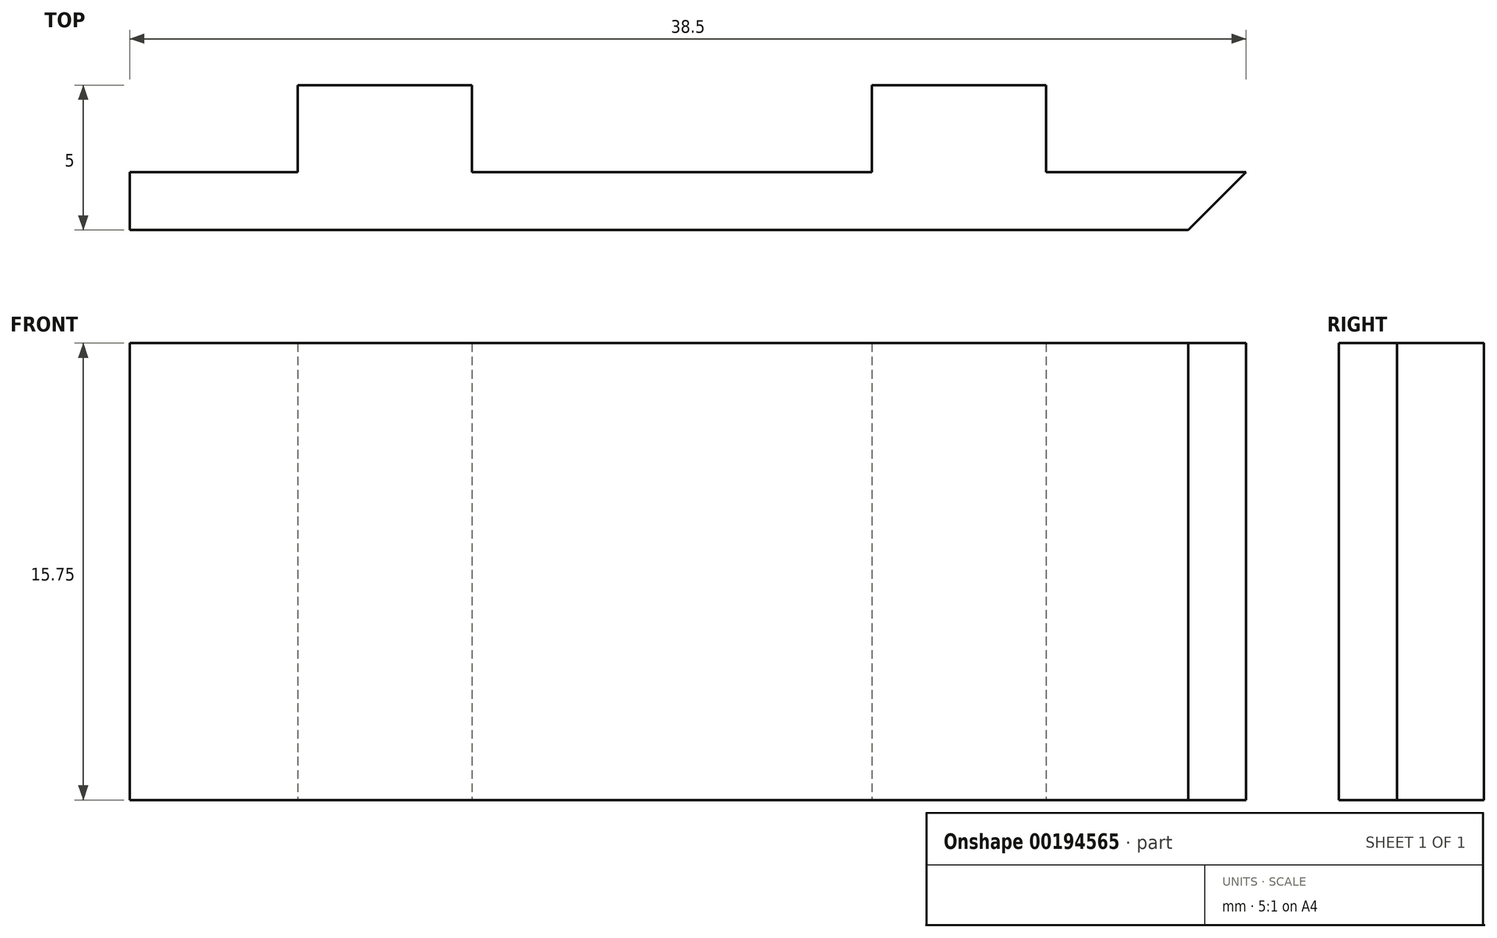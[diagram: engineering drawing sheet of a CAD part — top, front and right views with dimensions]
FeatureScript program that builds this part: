
annotation { "Feature Type Name" : "Feature", "Feature Type Description" : "" }
export const myFeature = defineFeature(function(context is Context, id is Id, definition is map)
    precondition{}
    {
        {
            var Q0;
            Q0=qCreatedBy(makeId("Top.planeOp"),FACE);
            var sketch = newSketch(context, id + "F0", { "sketchPlane" : qUnion([Q0])});
            skLineSegment(sketch, "E0", {"start": v(44.5, 0) * mm, "end": v(44.5, 10) * mm});
            skLineSegment(sketch, "E1", {"start": v(44.5, 10) * mm, "end": v(37.6, 10) * mm});
            skLineSegment(sketch, "E2", {"start": v(37.6, 10) * mm, "end": v(37.6, 16) * mm});
            skLineSegment(sketch, "E3", {"start": v(37.6, 16) * mm, "end": v(31.6, 16) * mm});
            skLineSegment(sketch, "E4", {"start": v(31.6, 16) * mm, "end": v(31.6, 10) * mm});
            skLineSegment(sketch, "E5", {"start": v(31.6, 10) * mm, "end": v(17.8, 10) * mm});
            skLineSegment(sketch, "E6", {"start": v(17.8, 10) * mm, "end": v(17.8, 16) * mm});
            skLineSegment(sketch, "E7", {"start": v(17.8, 16) * mm, "end": v(11.8, 16) * mm});
            skLineSegment(sketch, "E8", {"start": v(11.8, 16) * mm, "end": v(11.8, 10) * mm});
            skLineSegment(sketch, "E9", {"start": v(11.8, 10) * mm, "end": v(0, 10) * mm});
            skLineSegment(sketch, "E10", {"start": v(0, 0) * mm, "end": v(44.5, 0) * mm});
            skLineSegment(sketch, "E11", {"start": v(0, 10) * mm, "end": v(0, 0) * mm});
            skSolve(sketch);
        }
        {
            var Q0;
            Q0 = qSketchRegion(id + "F0", true);
            extrude(context, id + "F1", {"entities" : qUnion([Q0]), "depth" : 15.75 * mm});
        }
        {
            var Q0;
            Q0=makeQuery(id+"F1.opExtrude","CAP_FACE",FACE,{"disambiguationData":[OSD([sQuery(id+"F0.wireOp",EDGE,"E0"),sQuery(id+"F0.wireOp",EDGE,"E1"),sQuery(id+"F0.wireOp",EDGE,"E2"),sQuery(id+"F0.wireOp",EDGE,"E3"),sQuery(id+"F0.wireOp",EDGE,"E4"),sQuery(id+"F0.wireOp",EDGE,"E5"),sQuery(id+"F0.wireOp",EDGE,"E6"),sQuery(id+"F0.wireOp",EDGE,"E7"),sQuery(id+"F0.wireOp",EDGE,"E8"),sQuery(id+"F0.wireOp",EDGE,"E9"),sQuery(id+"F0.wireOp",EDGE,"E10"),sQuery(id+"F0.wireOp",EDGE,"E11")])],"isStart":false});
            var sketch = newSketch(context, id + "F2", { "sketchPlane" : qUnion([Q0])});
            skPoint(sketch, "E12", {"position": v(24.7, 5) * mm});
            skPoint(sketch, "E12.positionSnap0", {"position": v(44.5, 5) * mm});
            skPoint(sketch, "E12.positionSnap1", {"position": v(24.7, 10) * mm});
            skSolve(sketch);
        }
        {
            var Q0;
            Q0=sQuery(id+"F2.wireOp",VERTEX,"E12");
            var Q1;
            Q1=makeQuery(id+"F1.opExtrude","SWEPT_BODY",BODY,{"disambiguationData":[OSD([sQuery(id+"F0.wireOp",EDGE,"E0"),sQuery(id+"F0.wireOp",EDGE,"E1"),sQuery(id+"F0.wireOp",EDGE,"E2"),sQuery(id+"F0.wireOp",EDGE,"E3"),sQuery(id+"F0.wireOp",EDGE,"E4"),sQuery(id+"F0.wireOp",EDGE,"E5"),sQuery(id+"F0.wireOp",EDGE,"E6"),sQuery(id+"F0.wireOp",EDGE,"E7"),sQuery(id+"F0.wireOp",EDGE,"E8"),sQuery(id+"F0.wireOp",EDGE,"E9"),sQuery(id+"F0.wireOp",EDGE,"E10"),sQuery(id+"F0.wireOp",EDGE,"E11")])]});
            hole(context, id + "F3", {"style" : HoleStyle.SIMPLE, "endStyle" : HoleEndStyle.THROUGH, "holeDiameter" : 4 * mm, "locations" : qUnion([Q0]), "scope" : qUnion([Q1]), "isTappedThrough" : true, "startStyle" : HoleStartStyle.PART});
        }
        {
            var Q0;
            Q0=makeQuery(id+"F1.opExtrude","SWEPT_FACE",FACE,{"disambiguationData":[OSD([sQuery(id+"F0.wireOp",EDGE,"E11")])]});
            extrude(context, id + "F4", {"entities" : qUnion([Q0]), "operationType" : NewBodyOperationType.ADD, "depth" : 3 * mm});
        }
        {
            var Q0;
            {var subQ0=sQuery(id+"F0.wireOp",EDGE,"E9");Q0=makeQuery(id+"F4.boolean.opBoolean","MERGE",FACE,{"derivedFrom":[makeQuery(id+"F1.opExtrude","SWEPT_FACE",FACE,{"disambiguationData":[OSD([subQ0])]}),makeQuery(id+"F4.opExtrude","SWEPT_FACE",FACE,{"disambiguationData":[OSD([subQ0,sQuery(id+"F0.wireOp",EDGE,"E11")])]})]});}
            var sketch = newSketch(context, id + "F5", { "sketchPlane" : qUnion([Q0])});
            skLineSegment(sketch, "E13", {"start": v(0, 0) * mm, "end": v(0, 15.75) * mm});
            skSolve(sketch);
        }
        {
            var Q0;
            {var subQ0=sQuery(id+"F5.wireOp",EDGE,"E13");Q0=makeQuery(id+"F5.imprint","IMPRINT",FACE,{"disambiguationData":[TD([[makeQuery(id+"F5.imprint","IMPRINT",EDGE,{"derivedFrom":subQ0}),-1.0]])]});}
            extrude(context, id + "F6", {"entities" : qUnion([Q0]), "operationType" : NewBodyOperationType.ADD, "depth" : 25 * mm});
        }
        {
            var Q0;
            Q0=makeQuery(id+"F6.opExtrude","SWEPT_FACE",FACE,{"disambiguationData":[OSD([sQuery(id+"F5.wireOp",EDGE,"E13")])]});
            var sketch = newSketch(context, id + "F7", { "sketchPlane" : qUnion([Q0])});
            skPoint(sketch, "E14", {"position": v(27.25, 7.88) * mm});
            skPoint(sketch, "E14.positionSnap0", {"position": v(35, 7.88) * mm});
            skPoint(sketch, "E15", {"position": v(17.75, 7.88) * mm});
            skLineSegment(sketch, "E16", {"start": v(27.25, 7.88) * mm, "end": v(35, 7.88) * mm, "construction": true});
            skLineSegment(sketch, "E17", {"start": v(17.75, 7.88) * mm, "end": v(10, 7.88) * mm, "construction": true});
            skSolve(sketch);
        }
        {
            var Q0;
            Q0=sQuery(id+"F7.wireOp",VERTEX,"E14");
            var Q1;
            Q1=sQuery(id+"F7.wireOp",VERTEX,"E15");
            var Q2;
            Q2=makeQuery(id+"F1.opExtrude","SWEPT_BODY",BODY,{"disambiguationData":[OSD([sQuery(id+"F0.wireOp",EDGE,"E0"),sQuery(id+"F0.wireOp",EDGE,"E1"),sQuery(id+"F0.wireOp",EDGE,"E2"),sQuery(id+"F0.wireOp",EDGE,"E3"),sQuery(id+"F0.wireOp",EDGE,"E4"),sQuery(id+"F0.wireOp",EDGE,"E5"),sQuery(id+"F0.wireOp",EDGE,"E6"),sQuery(id+"F0.wireOp",EDGE,"E7"),sQuery(id+"F0.wireOp",EDGE,"E8"),sQuery(id+"F0.wireOp",EDGE,"E9"),sQuery(id+"F0.wireOp",EDGE,"E10"),sQuery(id+"F0.wireOp",EDGE,"E11")])]});
            hole(context, id + "F8", {"style" : HoleStyle.SIMPLE, "endStyle" : HoleEndStyle.THROUGH, "holeDiameter" : 2 * mm, "locations" : qUnion([Q0, Q1]), "scope" : qUnion([Q2]), "isTappedThrough" : true, "startStyle" : HoleStartStyle.SKETCH});
        }
        {
            var Q0;
            {var subQ0=sQuery(id+"F0.wireOp",EDGE,"E11");var subQ1=sQuery(id+"F0.wireOp",EDGE,"E9");var subQ2=makeQuery(id+"F4.boolean.opBoolean","MERGE",EDGE,{"derivedFrom":[makeQuery(id+"F1.opExtrude","CAP_EDGE",EDGE,{"disambiguationData":[OSD([subQ1])],"isStart":false}),makeQuery(id+"F4.opExtrude","SWEPT_EDGE",EDGE,{"disambiguationData":[OSD([subQ1,subQ0]),TDD([makeQuery(id+"F1.opExtrude","CAP_VERTEX",VERTEX,{"disambiguationData":[OSD([subQ1,subQ0])],"isStart":false})])]})]});Q0=makeQuery(id+"F6.boolean.opBoolean","MERGE",FACE,{"derivedFrom":[makeQuery(id+"F4.boolean.opBoolean","MERGE",FACE,{"derivedFrom":[makeQuery(id+"F1.opExtrude","CAP_FACE",FACE,{"disambiguationData":[OSD([sQuery(id+"F0.wireOp",EDGE,"E0"),sQuery(id+"F0.wireOp",EDGE,"E1"),sQuery(id+"F0.wireOp",EDGE,"E2"),sQuery(id+"F0.wireOp",EDGE,"E3"),sQuery(id+"F0.wireOp",EDGE,"E4"),sQuery(id+"F0.wireOp",EDGE,"E5"),sQuery(id+"F0.wireOp",EDGE,"E6"),sQuery(id+"F0.wireOp",EDGE,"E7"),sQuery(id+"F0.wireOp",EDGE,"E8"),subQ1,sQuery(id+"F0.wireOp",EDGE,"E10"),subQ0])],"isStart":false}),makeQuery(id+"F4.opExtrude","SWEPT_FACE",FACE,{"disambiguationData":[OSD([subQ0]),TDD([makeQuery(id+"F1.opExtrude","CAP_EDGE",EDGE,{"disambiguationData":[OSD([subQ0])],"isStart":false})])]})]}),makeQuery(id+"F6.opExtrude","SWEPT_FACE",FACE,{"disambiguationData":[OSD([subQ1,subQ0]),TDD([makeQuery(id+"F5.imprint","IMPRINT",EDGE,{"disambiguationData":[TD([[makeQuery(id+"F5.imprint","INTERSECT",VERTEX,{"derivedFrom":[subQ2,sQuery(id+"F5.wireOp",EDGE,"E13")]}),-1.0]])],"derivedFrom":subQ2})])]})]});}
            var sketch = newSketch(context, id + "F9", { "sketchPlane" : qUnion([Q0])});
            skLineSegment(sketch, "E18", {"start": v(0, 10) * mm, "end": v(0, 6) * mm});
            skLineSegment(sketch, "E19", {"start": v(0, 6) * mm, "end": v(6, 6) * mm});
            skLineSegment(sketch, "E20", {"start": v(6, 6) * mm, "end": v(6, 10) * mm});
            skLineSegment(sketch, "E21", {"start": v(6, 10) * mm, "end": v(0, 10) * mm});
            skSolve(sketch);
        }
        {
            var Q0;
            Q0 = qSketchRegion(id + "F9", true);
            extrude(context, id + "F10", {"entities" : qUnion([Q0]), "operationType" : NewBodyOperationType.REMOVE, "endBound" : BoundingType.THROUGH_ALL, "oppositeDirection" : true, "depth" : 25 * mm});
        }
        {
            var Q0;
            Q0=makeQuery(id+"F1.opExtrude","SWEPT_EDGE",EDGE,{"disambiguationData":[OSD([sQuery(id+"F0.wireOp",EDGE,"E7"),sQuery(id+"F0.wireOp",EDGE,"E8")])]});
            var Q1;
            Q1=makeQuery(id+"F1.opExtrude","SWEPT_EDGE",EDGE,{"disambiguationData":[OSD([sQuery(id+"F0.wireOp",EDGE,"E6"),sQuery(id+"F0.wireOp",EDGE,"E7")])]});
            var Q2;
            Q2=makeQuery(id+"F1.opExtrude","SWEPT_EDGE",EDGE,{"disambiguationData":[OSD([sQuery(id+"F0.wireOp",EDGE,"E3"),sQuery(id+"F0.wireOp",EDGE,"E4")])]});
            var Q3;
            Q3=makeQuery(id+"F1.opExtrude","SWEPT_EDGE",EDGE,{"disambiguationData":[OSD([sQuery(id+"F0.wireOp",EDGE,"E2"),sQuery(id+"F0.wireOp",EDGE,"E3")])]});
            chamfer(context, id + "F11", {"entities" : qUnion([Q0, Q1, Q2, Q3]), "width" : 1 * mm, "tangentPropagation" : true});
        }
        {
            var Q0;
            Q0=makeQuery(id+"F1.opExtrude","SWEPT_EDGE",EDGE,{"disambiguationData":[OSD([sQuery(id+"F0.wireOp",EDGE,"E0"),sQuery(id+"F0.wireOp",EDGE,"E10")])]});
            chamfer(context, id + "F12", {"entities" : qUnion([Q0]), "width" : 5 * mm, "tangentPropagation" : true});
        }
        {
            var Q0;
            {var subQ0=sQuery(id+"F0.wireOp",EDGE,"E11");var subQ1=sQuery(id+"F0.wireOp",EDGE,"E9");Q0=makeQuery(id+"F6.boolean.opBoolean","MERGE",FACE,{"derivedFrom":[makeQuery(id+"F4.opExtrude","CAP_FACE",FACE,{"disambiguationData":[OSD([subQ0])],"isStart":false}),makeQuery(id+"F6.opExtrude","SWEPT_FACE",FACE,{"disambiguationData":[OSD([subQ1,subQ0]),TDD([makeQuery(id+"F5.imprint","IMPRINT",EDGE,{"derivedFrom":makeQuery(id+"F4.opExtrude","CAP_EDGE",EDGE,{"disambiguationData":[OSD([subQ1,subQ0])],"isStart":false})})])]})]});}
            extrude(context, id + "F13", {"entities" : qUnion([Q0]), "operationType" : NewBodyOperationType.ADD, "depth" : 1 * mm});
        }
        {
            var Q0;
            Q0=makeQuery(id+"F10.boolean.opBoolean","MERGE",FACE,{"derivedFrom":[makeQuery(id+"F6.opExtrude","SWEPT_FACE",FACE,{"disambiguationData":[OSD([sQuery(id+"F5.wireOp",EDGE,"E13")])]}),makeQuery(id+"F10.opExtrude","SWEPT_FACE",FACE,{"disambiguationData":[OSD([sQuery(id+"F9.wireOp",EDGE,"E18")])]})]});
            extrude(context, id + "F14", {"entities" : qUnion([Q0]), "operationType" : NewBodyOperationType.REMOVE, "oppositeDirection" : true, "depth" : 1 * mm});
        }
        {
            var Q0;
            {var subQ0=sQuery(id+"F0.wireOp",EDGE,"E11");var subQ1=sQuery(id+"F0.wireOp",EDGE,"E9");var subQ2=makeQuery(id+"F4.boolean.opBoolean","MERGE",EDGE,{"derivedFrom":[makeQuery(id+"F1.opExtrude","CAP_EDGE",EDGE,{"disambiguationData":[OSD([subQ1])],"isStart":false}),makeQuery(id+"F4.opExtrude","SWEPT_EDGE",EDGE,{"disambiguationData":[OSD([subQ1,subQ0]),TDD([makeQuery(id+"F1.opExtrude","CAP_VERTEX",VERTEX,{"disambiguationData":[OSD([subQ1,subQ0])],"isStart":false})])]})]});var subQ3=makeQuery(id+"F5.imprint","INTERSECT",VERTEX,{"derivedFrom":[makeQuery(id+"F4.opExtrude","CAP_EDGE",EDGE,{"disambiguationData":[OSD([subQ1,subQ0])],"isStart":false}),subQ2]});var subQ4=makeQuery(id+"F1.opExtrude","CAP_EDGE",EDGE,{"disambiguationData":[OSD([subQ0])],"isStart":false});Q0=makeQuery(id+"F13.boolean.opBoolean","MERGE",FACE,{"derivedFrom":[makeQuery(id+"F6.boolean.opBoolean","MERGE",FACE,{"derivedFrom":[makeQuery(id+"F4.boolean.opBoolean","MERGE",FACE,{"derivedFrom":[makeQuery(id+"F1.opExtrude","CAP_FACE",FACE,{"disambiguationData":[OSD([sQuery(id+"F0.wireOp",EDGE,"E0"),sQuery(id+"F0.wireOp",EDGE,"E1"),sQuery(id+"F0.wireOp",EDGE,"E2"),sQuery(id+"F0.wireOp",EDGE,"E3"),sQuery(id+"F0.wireOp",EDGE,"E4"),sQuery(id+"F0.wireOp",EDGE,"E5"),sQuery(id+"F0.wireOp",EDGE,"E6"),sQuery(id+"F0.wireOp",EDGE,"E7"),sQuery(id+"F0.wireOp",EDGE,"E8"),subQ1,sQuery(id+"F0.wireOp",EDGE,"E10"),subQ0])],"isStart":false}),makeQuery(id+"F4.opExtrude","SWEPT_FACE",FACE,{"disambiguationData":[OSD([subQ0]),TDD([subQ4])]})]}),makeQuery(id+"F6.opExtrude","SWEPT_FACE",FACE,{"disambiguationData":[OSD([subQ1,subQ0]),TDD([makeQuery(id+"F5.imprint","IMPRINT",EDGE,{"disambiguationData":[TD([[makeQuery(id+"F5.imprint","INTERSECT",VERTEX,{"derivedFrom":[subQ2,sQuery(id+"F5.wireOp",EDGE,"E13")]}),-1.0]])],"derivedFrom":subQ2})])]})]}),makeQuery(id+"F13.opExtrude","SWEPT_FACE",FACE,{"disambiguationData":[OSD([subQ1,subQ0]),TDD([makeQuery(id+"F6.boolean.opBoolean","MERGE",EDGE,{"derivedFrom":[makeQuery(id+"F4.opExtrude","CAP_EDGE",EDGE,{"disambiguationData":[OSD([subQ0]),TDD([subQ4])],"isStart":false}),makeQuery(id+"F6.opExtrude","SWEPT_EDGE",EDGE,{"disambiguationData":[OSD([subQ1,subQ0]),TDD([subQ3])]})]})])]})]});}
            var sketch = newSketch(context, id + "F15", { "sketchPlane" : qUnion([Q0])});
            skLineSegment(sketch, "E22.bottom", {"start": v(5.9, 13) * mm, "end": v(43, 13) * mm});
            skLineSegment(sketch, "E22.top", {"start": v(5.9, 24.45) * mm, "end": v(43, 24.45) * mm});
            skLineSegment(sketch, "E22.left", {"start": v(5.9, 13) * mm, "end": v(5.9, 24.45) * mm});
            skLineSegment(sketch, "E22.right", {"start": v(43, 13) * mm, "end": v(43, 24.45) * mm});
            skLineSegment(sketch, "E23.bottom", {"start": v(-12.85, -2.88) * mm, "end": v(6, -2.88) * mm});
            skLineSegment(sketch, "E23.top", {"start": v(-12.85, 35.56) * mm, "end": v(6, 35.56) * mm});
            skLineSegment(sketch, "E23.left", {"start": v(-12.85, -2.88) * mm, "end": v(-12.85, 35.56) * mm});
            skLineSegment(sketch, "E23.right", {"start": v(6, -2.88) * mm, "end": v(6, 35.56) * mm});
            skLineSegment(sketch, "E24.bottom", {"start": v(49.35, -4.45) * mm, "end": v(6, -4.45) * mm});
            skLineSegment(sketch, "E24.top", {"start": v(49.35, 8) * mm, "end": v(6, 8) * mm});
            skLineSegment(sketch, "E24.left", {"start": v(49.35, -4.45) * mm, "end": v(49.35, 8) * mm});
            skLineSegment(sketch, "E24.right", {"start": v(6, -4.45) * mm, "end": v(6, 8) * mm});
            skSolve(sketch);
        }
        {
            var Q0;
            Q0 = qSketchRegion(id + "F15", true);
            extrude(context, id + "F16", {"entities" : qUnion([Q0]), "operationType" : NewBodyOperationType.REMOVE, "endBound" : BoundingType.THROUGH_ALL, "oppositeDirection" : true, "depth" : 25 * mm});
        }
        {
            var Q0;
            Q0=makeQuery(id+"F16.boolean.opBoolean","COPY",EDGE,{"derivedFrom":makeQuery(id+"F16.opExtrude","SWEPT_EDGE",EDGE,{"disambiguationData":[OSD([sQuery(id+"F15.wireOp",EDGE,"E23.right"),sQuery(id+"F15.wireOp",EDGE,"E24.top"),sQuery(id+"F15.wireOp",EDGE,"E24.right")])]})});
            var Q1;
            Q1=makeQuery(id+"F16.boolean.opBoolean","INTERSECT",EDGE,{"derivedFrom":[makeQuery(id+"F1.opExtrude","SWEPT_FACE",FACE,{"disambiguationData":[OSD([sQuery(id+"F0.wireOp",EDGE,"E0")])]}),makeQuery(id+"F16.opExtrude","SWEPT_FACE",FACE,{"disambiguationData":[OSD([sQuery(id+"F15.wireOp",EDGE,"E24.top")])]})]});
            chamfer(context, id + "F17", {"entities" : qUnion([Q0, Q1]), "width" : 2 * mm, "tangentPropagation" : true});
        }
    });
